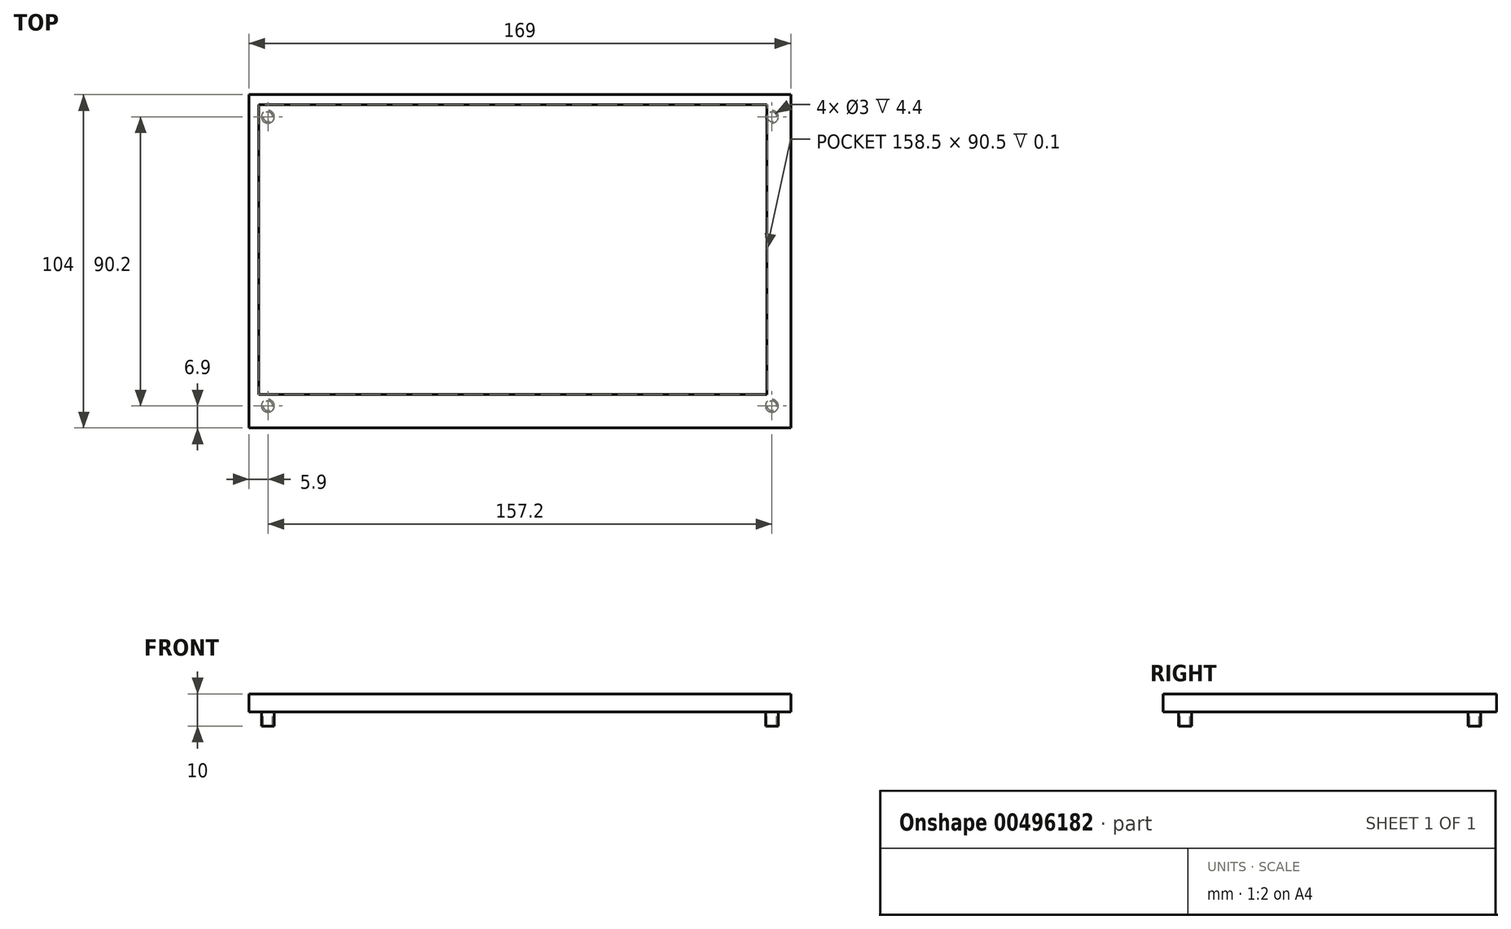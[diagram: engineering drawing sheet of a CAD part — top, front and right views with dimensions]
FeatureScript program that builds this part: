
annotation { "Feature Type Name" : "Feature", "Feature Type Description" : "" }
export const myFeature = defineFeature(function(context is Context, id is Id, definition is map)
    precondition{}
    {
        {
            var Q0;
            Q0=qCreatedBy(makeId("Top.planeOp"),FACE);
            var sketch = newSketch(context, id + "F0", { "sketchPlane" : qUnion([Q0])});
            skLineSegment(sketch, "E0.bottom", {"start": v(0, 0) * mm, "end": v(169, 0) * mm});
            skLineSegment(sketch, "E0.top", {"start": v(0, 104) * mm, "end": v(169, 104) * mm});
            skLineSegment(sketch, "E0.left", {"start": v(0, 0) * mm, "end": v(0, 104) * mm});
            skLineSegment(sketch, "E0.right", {"start": v(169, 0) * mm, "end": v(169, 104) * mm});
            skSolve(sketch);
        }
        {
            var Q0;
            Q0 = qSketchRegion(id + "F0", true);
            extrude(context, id + "F1", {"entities" : qUnion([Q0]), "depth" : 5.6 * mm});
        }
        {
            var Q0;
            Q0=makeQuery(id+"F1.opExtrude","CAP_FACE",FACE,{"disambiguationData":[OSD([sQuery(id+"F0.wireOp",EDGE,"E0.bottom"),sQuery(id+"F0.wireOp",EDGE,"E0.top"),sQuery(id+"F0.wireOp",EDGE,"E0.left"),sQuery(id+"F0.wireOp",EDGE,"E0.right")])],"isStart":false});
            var sketch = newSketch(context, id + "F2", { "sketchPlane" : qUnion([Q0])});
            skLineSegment(sketch, "E1.bottom", {"start": v(3.1, 100.9) * mm, "end": v(161.6, 100.9) * mm});
            skLineSegment(sketch, "E1.top", {"start": v(3.1, 10.4) * mm, "end": v(161.6, 10.4) * mm});
            skLineSegment(sketch, "E1.left", {"start": v(3.1, 100.9) * mm, "end": v(3.1, 10.4) * mm});
            skLineSegment(sketch, "E1.right", {"start": v(161.6, 100.9) * mm, "end": v(161.6, 10.4) * mm});
            skSolve(sketch);
        }
        {
            var Q0;
            Q0 = qSketchRegion(id + "F2", true);
            extrude(context, id + "F3", {"entities" : qUnion([Q0]), "operationType" : NewBodyOperationType.REMOVE, "oppositeDirection" : true, "depth" : 0.1 * mm});
        }
        {
            var Q0;
            Q0=makeQuery(id+"F1.opExtrude","CAP_FACE",FACE,{"disambiguationData":[OSD([sQuery(id+"F0.wireOp",EDGE,"E0.bottom"),sQuery(id+"F0.wireOp",EDGE,"E0.top"),sQuery(id+"F0.wireOp",EDGE,"E0.left"),sQuery(id+"F0.wireOp",EDGE,"E0.right")])],"isStart":true});
            var sketch = newSketch(context, id + "F4", { "sketchPlane" : qUnion([Q0])});
            skLineSegment(sketch, "E2", {"start": v(84.5, -104) * mm, "end": v(84.5, 0) * mm, "construction": true});
            skLineSegment(sketch, "E3", {"start": v(169, -52) * mm, "end": v(0, -52) * mm, "construction": true});
            skCircle(sketch, "E4", {"center": v(163.1, -97.1) * mm, "radius": 2 * mm});
            skCircle(sketch, "E5", {"center": v(163.1, -97.1) * mm, "radius": 1.5 * mm});
            skCircle(sketch, "E6.MirrorC", {"center": v(5.9, -97.1) * mm, "radius": 1.5 * mm});
            skCircle(sketch, "E7.MirrorC", {"center": v(5.9, -97.1) * mm, "radius": 2 * mm});
            skCircle(sketch, "E8.MirrorC", {"center": v(5.9, -6.9) * mm, "radius": 2 * mm});
            skCircle(sketch, "E9.MirrorC", {"center": v(5.9, -6.9) * mm, "radius": 1.5 * mm});
            skCircle(sketch, "E10.MirrorC", {"center": v(163.1, -6.9) * mm, "radius": 1.5 * mm});
            skCircle(sketch, "E11.MirrorC", {"center": v(163.1, -6.9) * mm, "radius": 2 * mm});
            skSolve(sketch);
        }
        {
            var Q0;
            Q0 = qSketchRegion(id + "F4", true);
            extrude(context, id + "F5", {"entities" : qUnion([Q0]), "operationType" : NewBodyOperationType.ADD, "depth" : 4.4 * mm});
        }
    });
